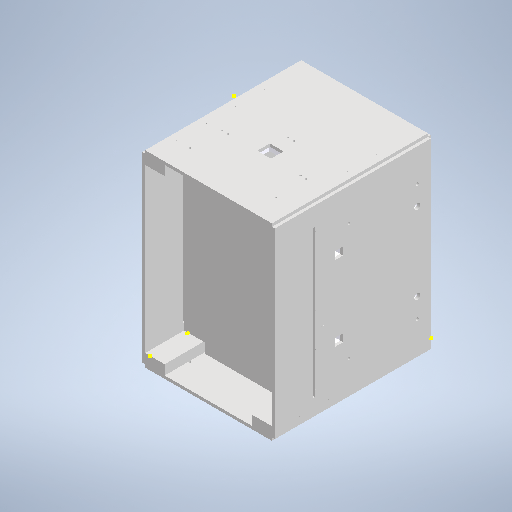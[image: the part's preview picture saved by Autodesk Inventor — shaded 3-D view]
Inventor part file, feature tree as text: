
AUTODESK INVENTOR PART (.ipt)
format: ipt  version: 2025.1 (Build 291241000, 241)  size: 1,091,072 bytes
history: native  units: mm
features: sketch x79, extrude x58, other x39, mirror x2, pattern_linear x1, imported_body x1
ambient origin geometry x8: Origin, YZ Plane, XZ Plane, XY Plane, X Axis, Y Axis, Z Axis, Center Point
bodies: Body1 (feature_tree), Body2 (feature_tree), Body3 (feature_tree), Body4 (feature_tree), Body5 (feature_tree), Body6 (feature_tree), Body7 (feature_tree), Body8 (feature_tree), Body9 (feature_tree), Body10 (feature_tree), Body11 (feature_tree), Body12 (feature_tree), Body13 (feature_tree), Body14 (feature_tree), Body15 (feature_tree), Body16 (feature_tree), Body17 (feature_tree), Body18 (feature_tree), Body19 (feature_tree), Body20 (feature_tree)
feature tree (180):
  other  "pilar 1"
  extrude  "Extrusão1"  Depth=100.0mm
  extrude  "Extrusão2"  Depth=935.0mm
  sketch  "Esboço3"  dims[d8=800.0mm d9=15.0mm d10=0.0mm]
  extrude  "Extrusão3"  Depth=15.0mm TaperAngle=0.0deg
  extrude  "Extrusão4"  Depth=50.0mm
  extrude  "Extrusão5"  Depth=650.0mm
  sketch  "Esboço8"  dims[d23=100.0mm d28=800.0mm d29=0.0mm]
  extrude  "Extrusão6"  Depth=15.0mm TaperAngle=0.0deg
  sketch  "Esboço10"  dims[d33=100.0mm d39=800.0mm d40=0.0mm]
  extrude  "Extrusão7"  Depth=800.0mm TaperAngle=0.0deg
  extrude  "Extrusão8"  Depth=15.0mm TaperAngle=0.0deg
  extrude  "Extrusão9"  Depth=800.0mm TaperAngle=0.0deg
  sketch  "Esboço14"  dims[d50=30.0mm d51=0.0mm d54=30.0mm d55=0.0mm]
  extrude  "Extrusão10"  Depth=15.0mm TaperAngle=0.0deg
  extrude  "Extrusão11"  Depth=30.0mm
  extrude  "Extrusão12"  Depth=600.0mm TaperAngle=0.0deg
  extrude  "Extrusão14"  Depth=30.0mm TaperAngle=0.0deg
  extrude  "Extrusão15"  Depth=500.0mm
  extrude  "Extrusão17"  Depth=30.0mm TaperAngle=0.0deg
  extrude  "Extrusão23"  Depth=875.0mm
  extrude  "Extrusão25"  Depth=45.0mm
  extrude  "Extrusão26"  Depth=30.0mm
  extrude  "Extrusão27"  Depth=30.0mm
  extrude  "Extrusão28"  Depth=400.0mm
  extrude  "Extrusão29"  Depth=3.5mm
  sketch  "Esboço39"  dims[d151=8000.0mm d152=0.0mm d163=3.5mm]
  extrude  "Extrusão30"  Depth=3.5mm
  sketch  "Esboço41"  dims[d167=3.5mm]
  sketch  "Esboço42"  dims[d169=3.5mm]
  extrude  "Extrusão32"  Depth=3.5mm
  extrude  "Extrusão33"  Depth=3.5mm
  extrude  "Extrusão34"  Depth=3.5mm
  extrude  "Extrusão35"  Depth=3.5mm
  pattern_linear  "Padrão retangular1"  Count1=800 Spacing1=0.0mm
  extrude  "Extrusão36"  Depth=3.5mm
  extrude  "Extrusão37"  Depth=3.5mm
  other  "Plano de trabalho1"
  mirror  "Espelhar2"
  mirror  "Espelhar3"
  sketch  "Esboço51"  dims[d208=3.5mm d209=0.0mm d216=20.0mm d217=0.0mm]
  sketch  "Esboço52"  dims[d218=15.0mm d219=0.0mm d220=15.0mm d221=0.0mm]
  sketch  "Esboço53"  dims[d222=15.0mm d223=7.5mm]
  sketch  "Esboço54"  dims[d224=935.0mm d225=467.5mm]
  extrude  "Extrusão39"  Depth=3.5mm TaperAngle=0.0deg
  sketch  "Esboço56"  dims[d231=40.0mm d232=958.0mm d233=0.0mm]
  extrude  "Extrusão40"  Depth=3.5mm
  extrude  "Extrusão41"  Depth=3.5mm
  extrude  "Extrusão42"  Depth=20.0mm TaperAngle=0.0deg
  sketch  "Esboço60"  dims[d242=100.0mm d243=15.0mm]
  extrude  "Extrusão43"  Depth=15.0mm TaperAngle=0.0deg
  sketch  "Esboço63"  dims[d249=20.0mm d250=6.0mm d251=0.0mm]
  sketch  "Esboço65"  dims[d252=95.0mm d253=15.0mm d254=0.0mm]
  extrude  "Extrusão45"  Depth=7.5mm
  sketch  "Esboço67"  dims[d259=10.0mm d260=5000.0mm d261=0.0mm]
  sketch  "Esboço68"  dims[d273=4.5mm d275=4.5mm]
  extrude  "Extrusão46"  Depth=467.5mm
  extrude  "Extrusão47"  Depth=50.0mm
  extrude  "Extrusão48"  Depth=40.0mm TaperAngle=0.0deg
  sketch  "Esboço73"  dims[d292=4.2mm d295=10.0mm d296=0.0mm]
  extrude  "Extrusão49"  Depth=45.0mm
  extrude  "Extrusão50"  Depth=200.0mm
  extrude  "Extrusão51"  Depth=30.0mm
  extrude  "Extrusão52"  Depth=15.0mm
  extrude  "Extrusão53"  Depth=20.0mm
  extrude  "Extrusão54"  Depth=6.0mm TaperAngle=0.0deg
  sketch  "Esboço80"  dims[d320=1910.5mm d321=0.0mm d322=70.0mm]
  extrude  "Extrusão55"  Depth=15.0mm TaperAngle=0.0deg
  extrude  "Extrusão56"  Depth=755.0mm
  extrude  "Extrusão57"  Depth=10.0mm TaperAngle=0.0deg
  extrude  "Extrusão58"  Depth=4.5mm
  extrude  "Extrusão59"  Depth=10.0mm TaperAngle=0.0deg
  extrude  "Extrusão60"  Depth=4.2mm
  extrude  "Extrusão61"  Depth=10.0mm TaperAngle=0.0deg
  sketch  "Esboço88"  dims[d352=20.0mm]
  extrude  "Extrusão62"  Depth=16.82mm
  extrude  "Extrusão63"  Depth=45.0mm TaperAngle=0.0deg
  extrude  "Extrusão64"  Depth=8.0mm
  sketch  "Esboço92"  dims[d358=3.5mm]
  extrude  "Extrusão66"  Depth=965.0mm TaperAngle=0.0deg
  extrude  "Extrusão67"  Depth=95.0mm
  extrude  "Extrusão68"  Depth=12.5mm
  sketch  "Esboço97"  dims[d368=4.0mm]
  extrude  "Extrusão69"  Depth=70.0mm
  extrude  "Extrusão70"  Depth=100.0mm
  sketch  "Esboço1"  dims[d1=50.0mm d2=100.0mm]
  sketch  "Esboço2"  dims[d4=800.0mm d5=0.0mm d7=935.0mm]
  other  "parede grande 1"
  sketch  "Esboço4"  dims[d11=100.0mm d12=50.0mm]
  other  "pilar 2"
  sketch  "Esboço6"  dims[d15=800.0mm d16=0.0mm d19=650.0mm]
  other  "parede pequena 1"
  sketch  "Esboço7"  dims[d20=800.0mm d21=15.0mm d22=0.0mm]
  other  "pilar 3"
  sketch  "Esboço9"  dims[d30=935.0mm d31=15.0mm d32=0.0mm]
  other  "parede grande 2"
  sketch  "Esboço11"  dims[d41=15.0mm d42=0.0mm d43=15.0mm d44=0.0mm]
  other  "pilar 4"
  sketch  "Esboço12"  dims[d45=600.0mm d46=30.0mm]
  other  "parede pequena 2"
  sketch  "Esboço13"  dims[d47=600.0mm d48=785.0mm d49=0.0mm]
  imported_body  "base"
  sketch  "Esboço15"  dims[d58=600.0mm d59=500.0mm]
  other  "isopor grande 1"
  sketch  "Esboço16"  dims[d60=600.0mm d61=30.0mm d62=0.0mm]
  other  "isoport grande 2"
  sketch  "Esboço17"  dims[d63=45.0mm d64=875.0mm]
  other  "isoport pequeno 1"
  sketch  "Esboço19"  dims[d65=15.0mm d66=0.0mm d71=45.0mm]
  other  "Contorno projetado4"
  other  "isopor pequeno 2"
  sketch  "Esboço20"  dims[d72=15.0mm d73=0.0mm d98=30.0mm]
  other  "moldura"
  sketch  "Esboço22"  dims[d99=585.0mm d100=0.0mm d104=30.0mm]
  sketch  "Esboço29"  dims[d105=585.0mm d106=0.0mm d111=400.0mm]
  other  "isopor interna 1"
  sketch  "Esboço31"  dims[d112=75.0mm d115=3.5mm]
  other  "isopor interno 2"
  sketch  "Esboço35"  dims[d119=3.5mm d123=3.5mm]
  sketch  "Esboço36"  dims[d127=3.5mm d131=3.5mm]
  sketch  "Esboço37"  dims[d132=8000.0mm d133=0.0mm d145=3.5mm]
  sketch  "Esboço38"  dims[d146=3.5mm d148=3.5mm]
  sketch  "Esboço40"  dims[d165=3.5mm]
  sketch  "Esboço45"  dims[d171=3.5mm d172=8000.0mm d173=0.0mm]
  other  "Contorno projetado8"
  other  "Contorno projetado9"
  other  "Contorno projetado10"
  other  "Contorno projetado11"
  sketch  "Esboço46"  dims[d184=3.5mm d186=3.5mm]
  other  "Contorno projetado12"
  sketch  "Esboço47"  dims[d188=3.5mm d190=3.5mm]
  other  "Contorno projetado13"
  sketch  "Esboço48"  dims[d192=3.5mm d193=8000.0mm d194=0.0mm]
  other  "Contorno projetado14"
  sketch  "Esboço49"  dims[d198=3.5mm d201=3.5mm]
  other  "Referência1"
  other  "Referência2"
  other  "Referência3"
  other  "Referência4"
  other  "Referência5"
  sketch  "Esboço50"  dims[d204=3.5mm d207=3.5mm]
  sketch  "Esboço55"  dims[d226=958.0mm d227=0.0mm d228=50.0mm d230=175.0mm]
  sketch  "Esboço57"  dims[d234=45.0mm d235=45.0mm]
  other  "vidro"
  sketch  "Esboço58"  dims[d236=5000.0mm d237=0.0mm d239=200.0mm]
  sketch  "Esboço59"  dims[d240=70.0mm d241=30.0mm]
  sketch  "Esboço61"  dims[d246=30.0mm d247=0.0mm d248=20.0mm]
  sketch  "Esboço66"  dims[d255=15.0mm d256=0.0mm d258=755.0mm]
  sketch  "Esboço69"  dims[d276=5000.0mm d277=0.0mm d280=10.0mm d281=0.0mm]
  sketch  "Esboço72"  dims[d285=4.2mm d286=4.2mm]
  sketch  "Esboço74"  dims[d297=16.82mm d298=16.82mm]
  sketch  "Esboço75"  dims[d300=15.0mm d301=45.0mm d302=0.0mm]
  sketch  "Esboço76"  dims[d304=8.0mm d306=8.0mm]
  sketch  "Esboço77"  dims[d307=40000.0mm d308=0.0mm d313=965.0mm d314=0.0mm]
  sketch  "Esboço78"  dims[d316=75.0mm d317=95.0mm]
  other  "Sólido21"
  sketch  "Esboço79"  dims[d318=85.0mm d319=12.5mm]
  sketch  "Esboço81"  dims[d323=100.0mm d324=167.5mm]
  other  "interno mdf"
  sketch  "Esboço82"  dims[d325=350.0mm]
  other  "Sólido24"
  sketch  "Esboço83"  dims[d328=15.0mm]
  other  "Sólido25"
  sketch  "Esboço84"  dims[d330=30.0mm]
  sketch  "Esboço85"  dims[d332=15.0mm]
  sketch  "Esboço86"  dims[d333=45.0mm d334=0.0mm]
  sketch  "Esboço87"  dims[d350=45000.0mm d351=0.0mm]
  sketch  "Esboço89"  dims[d353=20.0mm]
  sketch  "Esboço90"  dims[d354=62.0mm]
  sketch  "Esboço91"  dims[d355=62.0mm]
  sketch  "Esboço94"  dims[d361=3.5mm]
  sketch  "Esboço95"  dims[d364=3.5mm]
  sketch  "Esboço96"  dims[d367=3.5mm]
  other  "Sólido26"
  sketch  "Esboço98"  dims[d369=75.0mm]
  sketch  "Esboço99"  dims[d370=75.0mm d371=75.0mm d372=2000.0mm d373=0.0mm d374=50.0mm d376=75.0mm d377=20.0mm d378=409.03mm d379=16.0mm d380=650.0mm d381=0.0mm d382=30.0mm d383=0.0mm d384=30.0mm d385=0.0mm d386=50000.0mm d387=0.0mm d388=4.513mm d389=4.513mm d390=11.51mm d391=5000.0mm d392=5.0mm d393=0.0mm d394=0.0mm d395=4.513mm d396=4.513mm d397=11.51mm d398=33.595mm d399=33.595mm d400=239.566mm d401=5000.0mm d402=5.0mm d403=0.0mm d404=0.0mm d405=239.566mm d406=11.51mm d407=34.468mm d408=15.0mm d409=7.5mm d410=17.234mm d411=5000.0mm d412=0.0mm d413=34.468mm d414=15.0mm d415=42.5mm d416=13.842mm d417=5000.0mm d418=0.0mm d419=4.531mm d420=4.531mm d421=11.51mm d422=5.724mm d423=5000.0mm d424=0.0mm d431=40.0mm d432=2.398mm d433=40.0mm d434=2.398mm d435=40.0mm d436=5000.0mm d437=0.0mm d438=40.0mm d439=40.0mm d440=40.0mm d442=2.398mm d443=5000.0mm d444=0.0mm d452=1000.0mm d453=0.0mm d454=75.0mm d455=75.0mm d456=75.0mm d457=10.0mm d458=10.0mm d459=10.0mm d460=10.0mm d461=30.0mm d462=2000.0mm d463=0.0mm d464=10.0mm d465=10.0mm d466=10.0mm d467=30.0mm d468=10.0mm d469=10.0mm d470=2000.0mm d471=0.0mm d472=105.0mm d473=105.0mm d474=15.0mm d475=0.0mm d478=695.0mm d480=15.0mm d481=0.0mm d483=175.0mm d484=175.0mm d485=20.0mm d486=175.0mm d487=175.0mm d489=6.0mm d490=0.0mm d17=0.5mm d18=0.872665mm d79=0.5mm d80=0.872665mm d81=0.5mm d82=0.872665mm d262=0.5mm d263=0.872665mm d450=0.5mm d451=0.872665mm]
  other  "Sólido27"
  other  "<userpath>\Documents\1-CoisasSerias\UTFPR\2024-2\Oficina\Estrutura\Montagem1 - Copia.iam"
  other  "Montagem1 - Copia.iam"
  other  "cooler 40x40:1"
